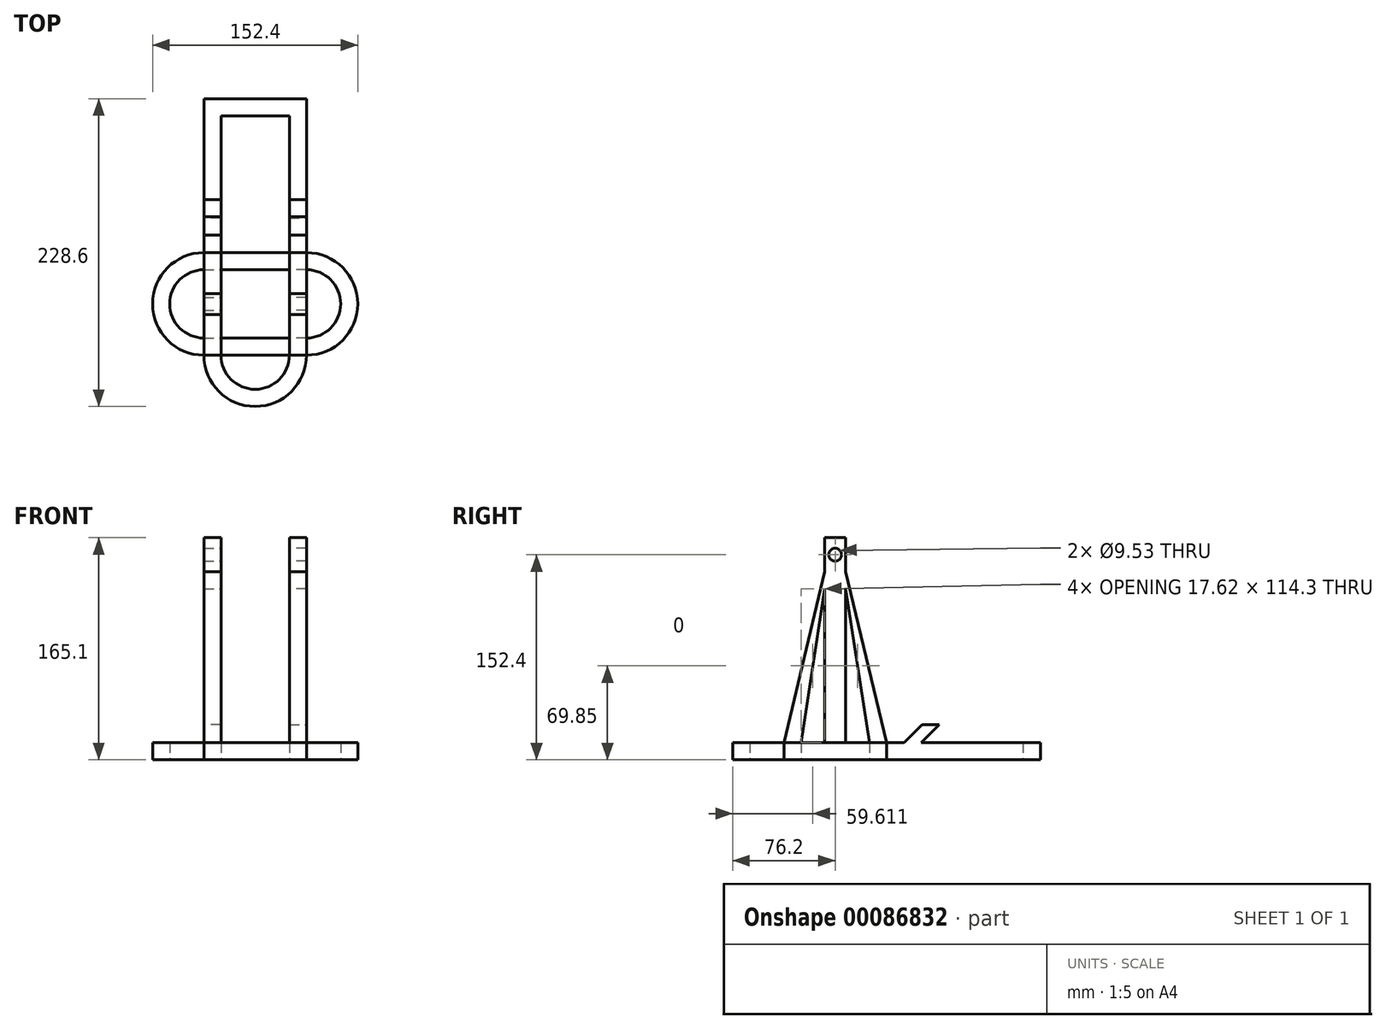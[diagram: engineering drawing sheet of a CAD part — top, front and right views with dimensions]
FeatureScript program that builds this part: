
annotation { "Feature Type Name" : "Feature", "Feature Type Description" : "" }
export const myFeature = defineFeature(function(context is Context, id is Id, definition is map)
    precondition{}
    {
        {
            var Q0;
            Q0=qCreatedBy(makeId("Top.planeOp"),FACE);
            var sketch = newSketch(context, id + "F0", { "sketchPlane" : qUnion([Q0])});
            skLineSegment(sketch, "E0.bottom", {"start": v(25.4, 38.1) * mm, "end": v(-25.4, 38.1) * mm});
            skLineSegment(sketch, "E0.top", {"start": v(38.1, -38.1) * mm, "end": v(-38.1, -38.1) * mm});
            skPoint(sketch, "E0.middle", {"position": v(0, 0) * mm});
            skArc(sketch, "E1", {"start": v(-38.1, 38.1) * mm, "mid": v(-76.2, 0) * mm, "end": v(-38.1, -38.1) * mm});
            skArc(sketch, "E2", {"start": v(38.1, -38.1) * mm, "mid": v(76.2, 0) * mm, "end": v(38.1, 38.1) * mm});
            skLineSegment(sketch, "E3.bottom", {"start": v(25.4, 25.4) * mm, "end": v(-25.4, 25.4) * mm});
            skLineSegment(sketch, "E3.top", {"start": v(25.4, -25.4) * mm, "end": v(-25.4, -25.4) * mm});
            skLineSegment(sketch, "E3.left", {"start": v(25.4, 25.4) * mm, "end": v(25.4, -25.4) * mm});
            skLineSegment(sketch, "E3.right", {"start": v(-25.4, 25.4) * mm, "end": v(-25.4, -25.4) * mm});
            skLineSegment(sketch, "E4", {"start": v(-38.1, 0) * mm, "end": v(-25.4, 0) * mm, "construction": true});
            skArc(sketch, "E5", {"start": v(-38.1, 25.4) * mm, "mid": v(-63.5, 0) * mm, "end": v(-38.1, -25.4) * mm});
            skArc(sketch, "E6", {"start": v(38.1, -25.4) * mm, "mid": v(63.5, 0) * mm, "end": v(38.1, 25.4) * mm});
            skLineSegment(sketch, "E7", {"start": v(-38.1, 25.4) * mm, "end": v(-38.1, -25.4) * mm});
            skLineSegment(sketch, "E8", {"start": v(38.1, 25.4) * mm, "end": v(38.1, -25.4) * mm});
            skLineSegment(sketch, "E9", {"start": v(25.4, 0) * mm, "end": v(38.1, 0) * mm});
            skLineSegment(sketch, "E10", {"start": v(0, 25.4) * mm, "end": v(0, 38.1) * mm, "construction": true});
            skLineSegment(sketch, "E11", {"start": v(-38.1, 38.1) * mm, "end": v(-38.1, 152.4) * mm});
            skLineSegment(sketch, "E12", {"start": v(25.4, 38.1) * mm, "end": v(25.4, 139.7) * mm});
            skLineSegment(sketch, "E13", {"start": v(38.1, 152.4) * mm, "end": v(38.1, 38.1) * mm});
            skLineSegment(sketch, "E14", {"start": v(-25.4, 139.7) * mm, "end": v(25.4, 139.7) * mm});
            skLineSegment(sketch, "E15.trimOffspring", {"start": v(-25.4, 139.7) * mm, "end": v(-25.4, 38.1) * mm});
            skLineSegment(sketch, "E16", {"start": v(0, 152.4) * mm, "end": v(0, 139.7) * mm});
            skLineSegment(sketch, "E17", {"start": v(-38.1, 152.4) * mm, "end": v(38.1, 152.4) * mm});
            skArc(sketch, "E18", {"start": v(-38.1, -38.1) * mm, "mid": v(0, -76.2) * mm, "end": v(38.1, -38.1) * mm});
            skArc(sketch, "E19", {"start": v(-25.4, -38.1) * mm, "mid": v(0, -63.5) * mm, "end": v(25.4, -38.1) * mm});
            skSolve(sketch);
        }
        {
            var Q0;
            Q0=makeQuery(id+"F0.imprint","IMPRINT",FACE,{"disambiguationData":[TD([[makeQuery(id+"F0.imprint","IMPRINT",EDGE,{"derivedFrom":sQuery(id+"F0.wireOp",EDGE,"E0.bottom")}),1.0]])]});
            var Q1;
            {var subQ0=sQuery(id+"F0.wireOp",EDGE,"E18");Q1=makeQuery(id+"F0.imprint","IMPRINT",FACE,{"disambiguationData":[TD([[makeQuery(id+"F0.imprint","IMPRINT",EDGE,{"derivedFrom":subQ0}),1.0]])]});}
            extrude(context, id + "F1", {"entities" : qUnion([Q0, Q1]), "depth" : 12.7 * mm});
        }
        {
            var Q0;
            Q0=makeQuery(id+"F1.opExtrude","CAP_FACE",FACE,{"disambiguationData":[OSD([sQuery(id+"F0.wireOp",EDGE,"E0.bottom"),sQuery(id+"F0.wireOp",EDGE,"E0.top"),sQuery(id+"F0.wireOp",EDGE,"E1"),sQuery(id+"F0.wireOp",EDGE,"E2"),sQuery(id+"F0.wireOp",EDGE,"E3.bottom"),sQuery(id+"F0.wireOp",EDGE,"E3.top"),sQuery(id+"F0.wireOp",EDGE,"E3.left"),sQuery(id+"F0.wireOp",EDGE,"E3.right"),sQuery(id+"F0.wireOp",EDGE,"E5"),sQuery(id+"F0.wireOp",EDGE,"E6"),sQuery(id+"F0.wireOp",EDGE,"E7"),sQuery(id+"F0.wireOp",EDGE,"E8"),sQuery(id+"F0.wireOp",EDGE,"E11"),sQuery(id+"F0.wireOp",EDGE,"eW0WrqK1-UAqt-hDgT-Up3a-L5sfFXZvn6og"),sQuery(id+"F0.wireOp",EDGE,"nnrCkwNE-DQRG-QEbR-UNsG-ga2bjcPdERez"),sQuery(id+"F0.wireOp",EDGE,"E12"),sQuery(id+"F0.wireOp",EDGE,"791204e0-3bb4-4a5e-b6f0-b63506c0d2d2"),sQuery(id+"F0.wireOp",EDGE,"E13"),sQuery(id+"F0.wireOp",EDGE,"E14"),sQuery(id+"F0.wireOp",EDGE,"Wew7rHin-LhuC-XoIG-YuWZ-GYeJMTqJVveu"),sQuery(id+"F0.wireOp",EDGE,"E15.trimOffspring"),sQuery(id+"F0.wireOp",EDGE,"b8e2c5c2-e6a5-42de-99a1-57f889a17564.trimOffspring")])],"isStart":false});
            var sketch = newSketch(context, id + "F2", { "sketchPlane" : qUnion([Q0])});
            skLineSegment(sketch, "E20.bottom", {"start": v(-25.4, 7.78) * mm, "end": v(-38.1, 7.78) * mm});
            skLineSegment(sketch, "E20.top", {"start": v(-25.4, -7.78) * mm, "end": v(-38.1, -7.78) * mm});
            skLineSegment(sketch, "E20.left", {"start": v(-25.4, 7.78) * mm, "end": v(-25.4, -7.78) * mm});
            skLineSegment(sketch, "E20.right", {"start": v(-38.1, 7.78) * mm, "end": v(-38.1, -7.78) * mm});
            skPoint(sketch, "E20.middle", {"position": v(-31.75, 0) * mm});
            skSolve(sketch);
        }
        {
            var Q0;
            Q0 = qSketchRegion(id + "F2", true);
            extrude(context, id + "F3", {"entities" : qUnion([Q0]), "operationType" : NewBodyOperationType.ADD, "depth" : 152.4 * mm});
        }
        {
            var Q0;
            Q0=makeQuery(id+"F3.opExtrude","SWEPT_FACE",FACE,{"disambiguationData":[OSD([sQuery(id+"F2.wireOp",EDGE,"E20.top")])]});
            var sketch = newSketch(context, id + "F4", { "sketchPlane" : qUnion([Q0])});
            skLineSegment(sketch, "E21.bottom", {"start": v(-38.1, 139.7) * mm, "end": v(-25.4, 139.7) * mm});
            skLineSegment(sketch, "E21.top", {"start": v(-38.1, 127) * mm, "end": v(-25.4, 127) * mm});
            skLineSegment(sketch, "E21.left", {"start": v(-38.1, 139.7) * mm, "end": v(-38.1, 127) * mm});
            skLineSegment(sketch, "E21.right", {"start": v(-25.4, 139.7) * mm, "end": v(-25.4, 127) * mm});
            skSolve(sketch);
        }
        {
            var Q0;
            Q0=makeQuery(id+"F3.opExtrude","SWEPT_FACE",FACE,{"disambiguationData":[OSD([sQuery(id+"F2.wireOp",EDGE,"E20.bottom")])]});
            var sketch = newSketch(context, id + "F5", { "sketchPlane" : qUnion([Q0])});
            skLineSegment(sketch, "E22.0", {"start": v(25.4, 139.7) * mm, "end": v(25.4, 127) * mm});
            skLineSegment(sketch, "E23.0", {"start": v(38.1, 139.7) * mm, "end": v(25.4, 139.7) * mm});
            skLineSegment(sketch, "E24.0", {"start": v(38.1, 127) * mm, "end": v(25.4, 127) * mm});
            skLineSegment(sketch, "E25.0", {"start": v(38.1, 139.7) * mm, "end": v(38.1, 127) * mm});
            skSolve(sketch);
        }
        {
            var Q0;
            Q0=makeQuery(id+"F1.opExtrude","CAP_FACE",FACE,{"disambiguationData":[OSD([sQuery(id+"F0.wireOp",EDGE,"E0.bottom"),sQuery(id+"F0.wireOp",EDGE,"E0.top"),sQuery(id+"F0.wireOp",EDGE,"E1"),sQuery(id+"F0.wireOp",EDGE,"E2"),sQuery(id+"F0.wireOp",EDGE,"E3.bottom"),sQuery(id+"F0.wireOp",EDGE,"E3.top"),sQuery(id+"F0.wireOp",EDGE,"E3.left"),sQuery(id+"F0.wireOp",EDGE,"E3.right"),sQuery(id+"F0.wireOp",EDGE,"E5"),sQuery(id+"F0.wireOp",EDGE,"E6"),sQuery(id+"F0.wireOp",EDGE,"E7"),sQuery(id+"F0.wireOp",EDGE,"E8"),sQuery(id+"F0.wireOp",EDGE,"E11"),sQuery(id+"F0.wireOp",EDGE,"eW0WrqK1-UAqt-hDgT-Up3a-L5sfFXZvn6og"),sQuery(id+"F0.wireOp",EDGE,"nnrCkwNE-DQRG-QEbR-UNsG-ga2bjcPdERez"),sQuery(id+"F0.wireOp",EDGE,"E12"),sQuery(id+"F0.wireOp",EDGE,"791204e0-3bb4-4a5e-b6f0-b63506c0d2d2"),sQuery(id+"F0.wireOp",EDGE,"E13"),sQuery(id+"F0.wireOp",EDGE,"E14"),sQuery(id+"F0.wireOp",EDGE,"Wew7rHin-LhuC-XoIG-YuWZ-GYeJMTqJVveu"),sQuery(id+"F0.wireOp",EDGE,"E15.trimOffspring"),sQuery(id+"F0.wireOp",EDGE,"b8e2c5c2-e6a5-42de-99a1-57f889a17564.trimOffspring")])],"isStart":false});
            var sketch = newSketch(context, id + "F6", { "sketchPlane" : qUnion([Q0])});
            skPoint(sketch, "E26.oppositeSnap0", {"position": v(-25.4, -16.59) * mm});
            skLineSegment(sketch, "E26.bottom", {"start": v(-38.1, -25.4) * mm, "end": v(-25.4, -25.4) * mm});
            skLineSegment(sketch, "E26.top", {"start": v(-38.1, -38.1) * mm, "end": v(-25.4, -38.1) * mm});
            skLineSegment(sketch, "E26.left", {"start": v(-38.1, -25.4) * mm, "end": v(-38.1, -38.1) * mm});
            skLineSegment(sketch, "E26.right", {"start": v(-25.4, -25.4) * mm, "end": v(-25.4, -38.1) * mm});
            skLineSegment(sketch, "E27.bottom", {"start": v(-38.1, 38.1) * mm, "end": v(-25.4, 38.1) * mm});
            skLineSegment(sketch, "E27.top", {"start": v(-38.1, 25.4) * mm, "end": v(-25.4, 25.4) * mm});
            skLineSegment(sketch, "E27.left", {"start": v(-38.1, 38.1) * mm, "end": v(-38.1, 25.4) * mm});
            skLineSegment(sketch, "E27.right", {"start": v(-25.4, 38.1) * mm, "end": v(-25.4, 25.4) * mm});
            skArc(sketch, "E28.0", {"start": v(-38.1, 25.4) * mm, "mid": v(-63.5, 0) * mm, "end": v(-38.1, -25.4) * mm});
            skArc(sketch, "E29.0", {"start": v(-38.1, 38.1) * mm, "mid": v(-76.2, 0) * mm, "end": v(-38.1, -38.1) * mm});
            skSolve(sketch);
        }
        {
            var Q1;
            Q1=makeQuery(id+"F5.imprint","IMPRINT",FACE,{"disambiguationData":[TD([[makeQuery(id+"F5.imprint","IMPRINT",EDGE,{"derivedFrom":sQuery(id+"F5.wireOp",EDGE,"E22.0")}),1.0]])]});
            var Q2;
            Q2=makeQuery(id+"F6.imprint","IMPRINT",FACE,{"disambiguationData":[TD([[makeQuery(id+"F6.imprint","IMPRINT",EDGE,{"derivedFrom":sQuery(id+"F6.wireOp",EDGE,"E27.bottom")}),-1.0]])]});
            loft(context, id + "F7", {"operationType" : NewBodyOperationType.ADD, "sheetProfilesArray" : [{ "sheetProfileEntities" : qUnion([Q1]) }, { "sheetProfileEntities" : qUnion([Q2]) }]});
        }
        {
            var Q1;
            Q1=makeQuery(id+"F6.imprint","IMPRINT",FACE,{"disambiguationData":[TD([[makeQuery(id+"F6.imprint","IMPRINT",EDGE,{"derivedFrom":sQuery(id+"F6.wireOp",EDGE,"E26.bottom")}),-1.0]])]});
            var Q2;
            Q2=makeQuery(id+"F4.imprint","IMPRINT",FACE,{"disambiguationData":[TD([[makeQuery(id+"F4.imprint","IMPRINT",EDGE,{"derivedFrom":sQuery(id+"F4.wireOp",EDGE,"E21.bottom")}),-1.0]])]});
            loft(context, id + "F8", {"operationType" : NewBodyOperationType.ADD, "sheetProfilesArray" : [{ "sheetProfileEntities" : qUnion([Q1]) }, { "sheetProfileEntities" : qUnion([Q2]) }]});
        }
        {
            var Q0;
            Q0=makeQuery(id+"F1.opExtrude","SWEPT_FACE",FACE,{"disambiguationData":[OSD([sQuery(id+"F0.wireOp",EDGE,"E11")])]});
            var sketch = newSketch(context, id + "F9", { "sketchPlane" : qUnion([Q0])});
            skLineSegment(sketch, "E30", {"start": v(-63.94, 12.7) * mm, "end": v(-77.41, 26.17) * mm});
            skLineSegment(sketch, "E31", {"start": v(-77.41, 26.17) * mm, "end": v(-64.71, 26.17) * mm});
            skLineSegment(sketch, "E32", {"start": v(-64.71, 26.17) * mm, "end": v(-51.24, 12.7) * mm});
            skSolve(sketch);
        }
        {
            var Q0;
            {var subQ0=sQuery(id+"F9.wireOp",EDGE,"E30");Q0=makeQuery(id+"F9.imprint","IMPRINT",FACE,{"disambiguationData":[TD([[makeQuery(id+"F9.imprint","IMPRINT",EDGE,{"derivedFrom":subQ0}),-1.0]])]});}
            var Q1;
            Q1=makeQuery(id+"F1.opExtrude","SWEPT_FACE",FACE,{"disambiguationData":[OSD([sQuery(id+"F0.wireOp",EDGE,"E15.trimOffspring")])]});
            extrude(context, id + "F10", {"entities" : qUnion([Q0]), "operationType" : NewBodyOperationType.ADD, "endBound" : BoundingType.UP_TO_SURFACE, "oppositeDirection" : true, "endBoundEntityFace" : qUnion([Q1]), "depth" : 25.4 * mm});
        }
        {
            var Q0;
            {var subQ0=sQuery(id+"F2.wireOp",EDGE,"E20.left");var subQ1=sQuery(id+"F0.wireOp",EDGE,"E3.right");Q0=makeQuery(id+"F8.boolean.opBoolean","MERGE",FACE,{"derivedFrom":[makeQuery(id+"F7.boolean.opBoolean","MERGE",FACE,{"derivedFrom":[makeQuery(id+"F3.boolean.opBoolean","MERGE",FACE,{"derivedFrom":[makeQuery(id+"F1.opExtrude","SWEPT_FACE",FACE,{"disambiguationData":[OSD([subQ1])]}),makeQuery(id+"F3.opExtrude","SWEPT_FACE",FACE,{"disambiguationData":[OSD([subQ0])]})]}),makeQuery(id+"F7.opLoft","SWEPT_FACE",FACE,{"disambiguationData":[OSD([sQuery(id+"F0.wireOp",EDGE,"E0.bottom"),sQuery(id+"F0.wireOp",EDGE,"E3.bottom"),subQ1,sQuery(id+"F0.wireOp",EDGE,"E15.trimOffspring"),sQuery(id+"F2.wireOp",EDGE,"E20.bottom"),subQ0,sQuery(id+"F5.wireOp",EDGE,"E22.0"),sQuery(id+"F5.wireOp",EDGE,"E23.0"),sQuery(id+"F5.wireOp",EDGE,"E24.0"),sQuery(id+"F6.wireOp",EDGE,"E27.bottom"),sQuery(id+"F6.wireOp",EDGE,"E27.top"),sQuery(id+"F6.wireOp",EDGE,"E27.right")])]})]}),makeQuery(id+"F8.opLoft","SWEPT_FACE",FACE,{"disambiguationData":[OSD([sQuery(id+"F0.wireOp",EDGE,"E0.top"),sQuery(id+"F0.wireOp",EDGE,"E3.top"),subQ1,sQuery(id+"F0.wireOp",EDGE,"E19"),sQuery(id+"F2.wireOp",EDGE,"E20.top"),subQ0,sQuery(id+"F4.wireOp",EDGE,"E21.bottom"),sQuery(id+"F4.wireOp",EDGE,"E21.top"),sQuery(id+"F4.wireOp",EDGE,"E21.right"),sQuery(id+"F6.wireOp",EDGE,"E26.bottom"),sQuery(id+"F6.wireOp",EDGE,"E26.top"),sQuery(id+"F6.wireOp",EDGE,"E26.right")])]})]});}
            var sketch = newSketch(context, id + "F11", { "sketchPlane" : qUnion([Q0])});
            skLineSegment(sketch, "E33", {"start": v(0, 165.1) * mm, "end": v(0, 139.7) * mm, "construction": true});
            skCircle(sketch, "E34", {"center": v(0, 152.4) * mm, "radius": 4.76 * mm});
            skSolve(sketch);
        }
        {
            var Q0;
            Q0=makeQuery(id+"F11.imprint","IMPRINT",FACE,{"disambiguationData":[TD([[makeQuery(id+"F11.imprint","IMPRINT",EDGE,{"derivedFrom":sQuery(id+"F11.wireOp",EDGE,"E34")}),1.0]])]});
            var Q1;
            Q1=sQuery(id+"F11.wireOp",EDGE,"E34");
            extrude(context, id + "F12", {"entities" : qUnion([Q0]), "operationType" : NewBodyOperationType.REMOVE, "surfaceEntities" : qUnion([Q1]), "endBound" : BoundingType.THROUGH_ALL, "oppositeDirection" : true, "depth" : 25.4 * mm});
        }
        {
            var Q0;
            Q0=makeQuery(id+"F1.opExtrude","SWEPT_BODY",BODY,{"disambiguationData":[OSD([sQuery(id+"F0.wireOp",EDGE,"E0.bottom"),sQuery(id+"F0.wireOp",EDGE,"E0.top"),sQuery(id+"F0.wireOp",EDGE,"E1"),sQuery(id+"F0.wireOp",EDGE,"E2"),sQuery(id+"F0.wireOp",EDGE,"E3.bottom"),sQuery(id+"F0.wireOp",EDGE,"E3.top"),sQuery(id+"F0.wireOp",EDGE,"E3.left"),sQuery(id+"F0.wireOp",EDGE,"E3.right"),sQuery(id+"F0.wireOp",EDGE,"E5"),sQuery(id+"F0.wireOp",EDGE,"E6"),sQuery(id+"F0.wireOp",EDGE,"E7"),sQuery(id+"F0.wireOp",EDGE,"E8"),sQuery(id+"F0.wireOp",EDGE,"E11"),sQuery(id+"F0.wireOp",EDGE,"E12"),sQuery(id+"F0.wireOp",EDGE,"791204e0-3bb4-4a5e-b6f0-b63506c0d2d2"),sQuery(id+"F0.wireOp",EDGE,"E13"),sQuery(id+"F0.wireOp",EDGE,"E14"),sQuery(id+"F0.wireOp",EDGE,"Wew7rHin-LhuC-XoIG-YuWZ-GYeJMTqJVveu"),sQuery(id+"F0.wireOp",EDGE,"E15.trimOffspring"),sQuery(id+"F0.wireOp",EDGE,"b8e2c5c2-e6a5-42de-99a1-57f889a17564.trimOffspring"),sQuery(id+"F0.wireOp",EDGE,"2s5irlIo-1hsk-PBSL-bw71-EGN7Nmvhz8i4"),sQuery(id+"F0.wireOp",EDGE,"WOsVuXmC-js16-euqo-qlyW-9Vxgc6dwlDmT")])]});
            var Q1;
            Q1=qCreatedBy(makeId("Right.planeOp"),FACE);
            mirror(context, id + "F13", {"operationType" : NewBodyOperationType.ADD, "entities" : qUnion([Q0]), "mirrorPlane" : qUnion([Q1])});
        }
    });
